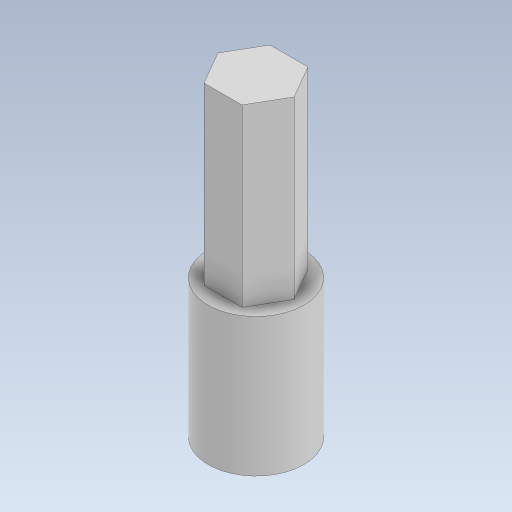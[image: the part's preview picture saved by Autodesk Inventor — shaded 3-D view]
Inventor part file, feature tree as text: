
AUTODESK INVENTOR PART (.ipt)
format: ipt  version: 2023.5 (Build 275446000, 446)  size: 321,024 bytes
history: native  units: mm
features: extrude x6, sketch x4, hole x1
ambient origin geometry x8: Origin, YZ Plane, XZ Plane, XY Plane, X Axis, Y Axis, Z Axis, Center Point
bodies: Solid1 (feature_tree), Solid2 (feature_tree)
feature tree (11):
  extrude  "Extrusion2"  Depth=2.38mm TaperAngle=0.0deg
  extrude  "Extrusion3"  Depth=7.0mm
  extrude  "Extrusion5"  Depth=9.0mm
  extrude  "Extrusion11"  Depth=4.4mm
  extrude  "Extrusion6"  Depth=3.5mm
  hole  "Hole1"  [1 undecoded]
  extrude  "Extrusion1"  Depth=7.16mm
  sketch  "Sketch7"  dims[d0=25.0mm d1=2.38mm d2=0.0mm]
  sketch  "Sketch9"  dims[d3=4.0mm d4=7.0mm]
  sketch  "Sketch10"  dims[d5=3.5mm d6=9.0mm]
  sketch  "Sketch15"  dims[d7=13.0mm d8=0.0mm d9=4.4mm d10=3.5mm d11=13.0mm d12=0.0mm d15=7.16mm d16=16.5mm d17=0.0mm d18=0.5mm d19=0.0mm d21=2.0mm d22=2.25mm d23=0.0mm d24=2.0mm d25=6.0mm d26=4.0mm d27=2.0mm d28=90.0deg d29=3.33mm d30=0.0mm d41=2.0mm d42=4.25mm d43=0.0mm d13=0.5mm d14=0.872665mm d34=0.5mm d35=0.872665mm d36=0.5mm d37=0.872665mm d38=0.5mm d39=0.872665mm d40=0.5mm]
note: 1 required parameter value undecoded (feature->parameter linkage not recoverable at this tier; creation-order binding heuristic only, values carry confidence <= 0.55)
